# Revit family: Toilet-Wall_Mount-KOHLER-REPLAY-K-6098IN
name_source: partatom
category: Plumbing Fixtures
revit_build: Autodesk Revit 2017 (Build: 20160225_1515(x64)
units: mm (PartAtom-declared; Revit-internal decimal feet)

## family parameters
Cut with Voids When Loaded = No
Host = Face
OmniClass Number = 23.31.19.00
OmniClass Title = Toilets
Part Type = Normal
Room Calculation Point = No
Round Connector Dimension = Use Diameter
Shared = No

## types (4) — shared parameters
ADA Compliant = No
Assembly Code = D2010100
CW Connection = Yes
Cold Water Inlet = Cold Water Inlet
Date Modified = 01/21/2021
Default Elevation = 0"
Flow Rate = 0 GPM
Flush Rate- GPF = GPF
Flush Rate- LPF = LPF
HW Connection = No
Height = 16 5/16"
Hot Water Inlet = Hot Water Inlet
Manufacturer = KOHLER Co.
Master Format 2014 = 22 42 13.13
Master Format 2014 Name = Residential Water Closets
Material = Vitreous China
Pressure = 0.00 psi
Product Name = REPLAY
Seat Included = Yes
URL = https://www.kohler.co.in
Vent Connection = No
Waste Connection = Yes
Waste Water Outlet = Waste Water Outlet
WaterSense Certified = No

## per-type parameters (varying)
| type | Description | Finish | K-6098IN-S | K-6098IN-SR | Length | Model | Product Page URL | Type | Width |
| Thick Regular Close Seat, 0-White | WALL HUNG BOWL W/ RC SEAT | Kohler-Vitreous_China-0-White | Yes | No | 21 9/16" | K-6098IN-0 |  | 1 | 14 15/16" |
| Thick Quite Close Seat, 0-White | Wall Hung Bowl w/ Qc Seat | Kohler-Vitreous_China-0-White | Yes | No | 21 9/16" | K-6098IN-S-0 | https://www.kohler.co.in | 2 | 14 15/16" |
| Thick Quite Close Seat, K4-Cashmere | Wall Hung Bowl w/ Qc Seat | Kohler-Vitreous_China-K4-Cashmere | Yes | No | 21 9/16" | K-6098IN-S-K4 | https://www.kohler.co.in | 3 | 14 15/16" |
| Thin Quite Close Seat, 0-White | Wall-Hung Toilet w/SC Slim Seat | Kohler-Vitreous_China-0-White | No | Yes | 21 5/16" | K-6098IN-SR-0 | https://www.kohler.co.in | 4 | 14 7/16" |

## geometry (parser evidence)
native form markers: Sweep x5
no freeform markers — native parametric forms only
